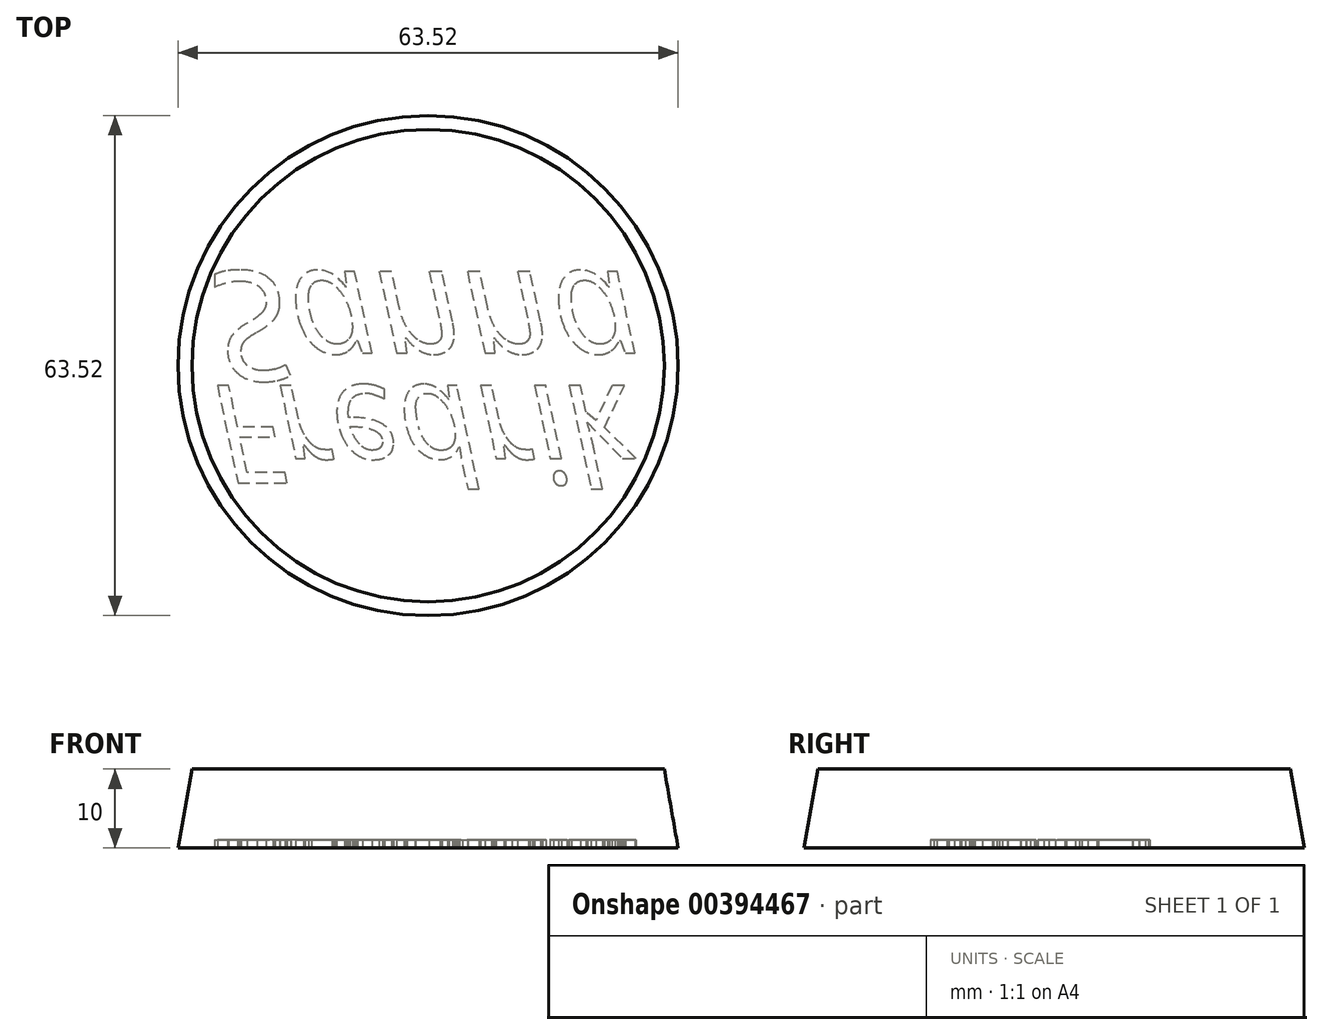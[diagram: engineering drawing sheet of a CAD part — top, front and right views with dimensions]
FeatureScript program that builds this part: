
annotation { "Feature Type Name" : "Feature", "Feature Type Description" : "" }
export const myFeature = defineFeature(function(context is Context, id is Id, definition is map)
    precondition{}
    {
        {
            var Q0;
            Q0=qCreatedBy(makeId("Top.planeOp"),FACE);
            var sketch = newSketch(context, id + "F0", { "sketchPlane" : qUnion([Q0])});
            skCircle(sketch, "E0", {"center": v(0, 0) * mm, "radius": 30 * mm});
            skSolve(sketch);
        }
        {
            var Q0;
            Q0=makeQuery(id+"F0.imprint","IMPRINT",FACE,{"disambiguationData":[TD([[makeQuery(id+"F0.imprint","IMPRINT",EDGE,{"derivedFrom":sQuery(id+"F0.wireOp",EDGE,"E0")}),1.0]])]});
            extrude(context, id + "F1", {"entities" : qUnion([Q0]), "oppositeDirection" : true, "depth" : 10 * mm, "hasDraft" : true, "draftAngle" : 10 * degree});
        }
        {
            var Q0;
            Q0=makeQuery(id+"F1.opExtrude","CAP_FACE",FACE,{"disambiguationData":[OSD([sQuery(id+"F0.wireOp",EDGE,"E0")])],"isStart":false});
            var sketch = newSketch(context, id + "F2", { "sketchPlane" : qUnion([Q0])});
            skText(sketch, "E1", { "text": "Fredrik", "fontName": "OpenSans-Italic.ttf"});
            skText(sketch, "E2", { "text": "Sanna", "fontName": "OpenSans-Italic.ttf"});
            const initialGuessF2  = {"E1": [-0.0275, 0.0025, 1, 0, 0.0125], "E2": [-0.0275, -0.01198, 1, 0, 0.01398]};
            skSetInitialGuess(sketch, initialGuessF2);
            skSolve(sketch);
        }
        {
            var Q0;
            Q0=qSketchRegion(id+"F2",true);
            extrude(context, id + "F3", {"entities" : qUnion([Q0]), "operationType" : NewBodyOperationType.REMOVE, "oppositeDirection" : true, "depth" : 1 * mm});
        }
    });
